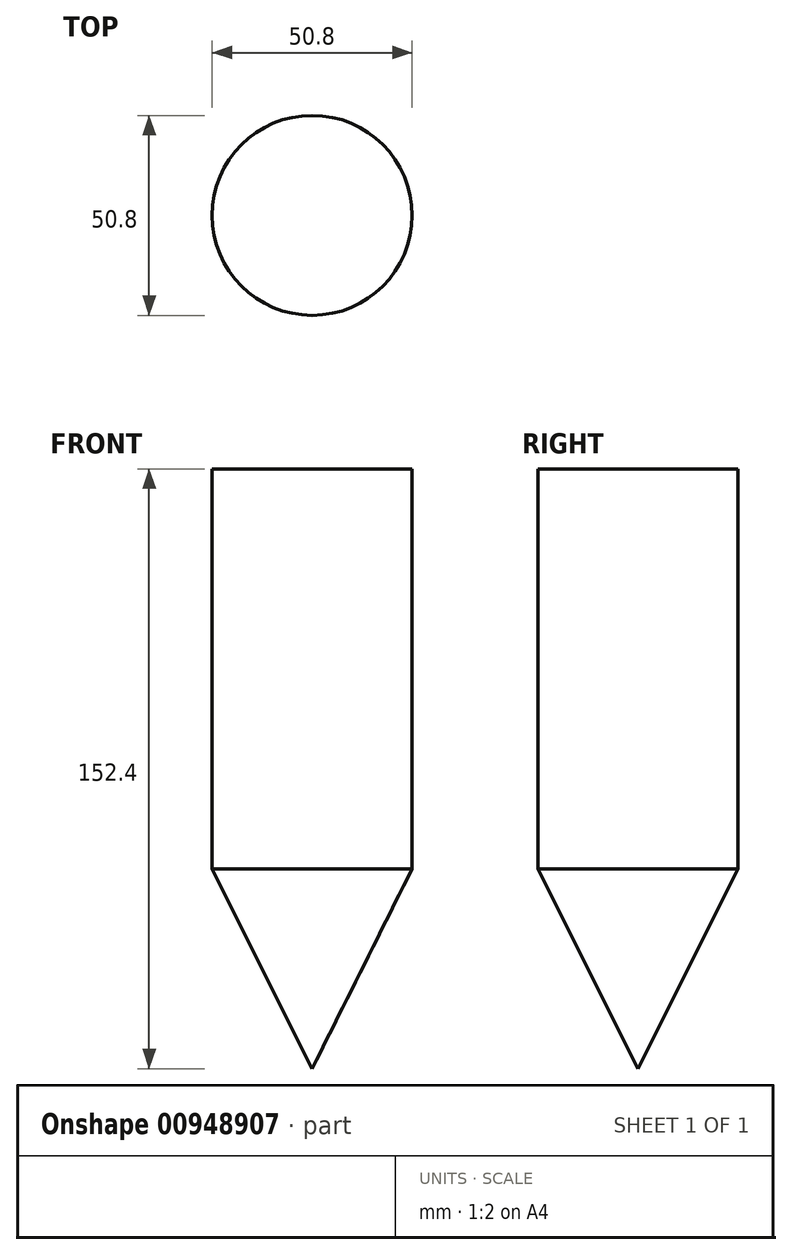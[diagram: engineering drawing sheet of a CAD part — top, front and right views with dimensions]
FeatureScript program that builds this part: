
annotation { "Feature Type Name" : "Feature", "Feature Type Description" : "" }
export const myFeature = defineFeature(function(context is Context, id is Id, definition is map)
    precondition{}
    {
        {
            var Q0;
            Q0=qCreatedBy(makeId("Front.planeOp"),FACE);
            var sketch = newSketch(context, id + "F0", { "sketchPlane" : qUnion([Q0])});
            skLineSegment(sketch, "E0", {"start": v(0, 0) * mm, "end": v(25.4, 0) * mm});
            skLineSegment(sketch, "E1", {"start": v(25.4, 0) * mm, "end": v(25.4, -101.6) * mm});
            skLineSegment(sketch, "E2", {"start": v(25.4, -101.6) * mm, "end": v(0, -152.4) * mm});
            skLineSegment(sketch, "E3", {"start": v(0, -152.4) * mm, "end": v(0, 0) * mm});
            skSolve(sketch);
        }
        {
            var Q0;
            Q0=makeQuery(id+"F0.imprint","IMPRINT",FACE,{"disambiguationData":[TD([[makeQuery(id+"F0.imprint","IMPRINT",EDGE,{"derivedFrom":sQuery(id+"F0.wireOp",EDGE,"E0")}),-1.0]])]});
            var Q1;
            Q1=sQuery(id+"F0.wireOp",EDGE,"E3");
            revolve(context, id + "F1", {"surfaceOperationType" : NewSurfaceOperationType.NEW, "entities" : qUnion([Q0]), "axis" : qUnion([Q1]), "revolveType" : RevolveType.FULL});
        }
    });
